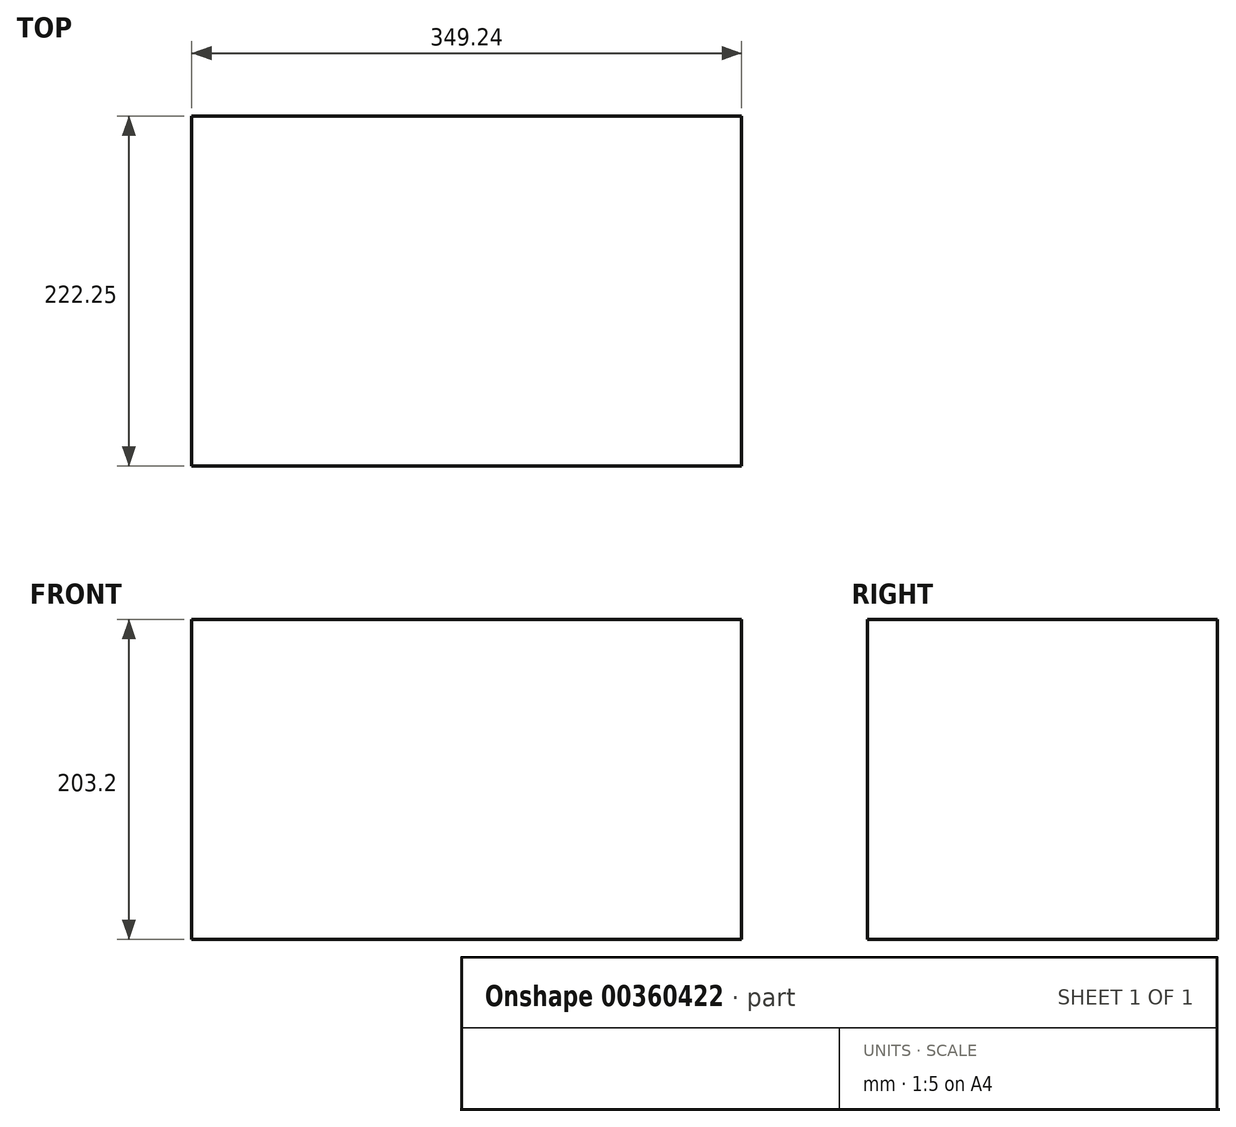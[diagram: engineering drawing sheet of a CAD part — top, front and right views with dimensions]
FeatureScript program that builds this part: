
annotation { "Feature Type Name" : "Feature", "Feature Type Description" : "" }
export const myFeature = defineFeature(function(context is Context, id is Id, definition is map)
    precondition{}
    {
        {
            var Q0;
            Q0=qCreatedBy(makeId("Top.planeOp"),FACE);
            var sketch = newSketch(context, id + "F0", { "sketchPlane" : qUnion([Q0])});
            skLineSegment(sketch, "E0.bottom", {"start": v(174.63, 109.93) * mm, "end": v(-174.63, 109.93) * mm});
            skLineSegment(sketch, "E0.top", {"start": v(174.63, -112.32) * mm, "end": v(-174.63, -112.32) * mm});
            skLineSegment(sketch, "E0.left", {"start": v(174.63, 109.93) * mm, "end": v(174.63, -112.32) * mm});
            skLineSegment(sketch, "E0.right", {"start": v(-174.63, 109.93) * mm, "end": v(-174.63, -112.32) * mm});
            skPoint(sketch, "E0.middle", {"position": v(0, -1.2) * mm});
            skSolve(sketch);
        }
        {
            var Q0;
            Q0=makeQuery(id+"F0.imprint","IMPRINT",FACE,{"disambiguationData":[TD([[makeQuery(id+"F0.imprint","IMPRINT",EDGE,{"derivedFrom":sQuery(id+"F0.wireOp",EDGE,"E0.bottom")}),1.0]])]});
            extrude(context, id + "F1", {"entities" : qUnion([Q0]), "endBound" : BoundingType.SYMMETRIC, "depth" : 203.2 * mm});
        }
    });
